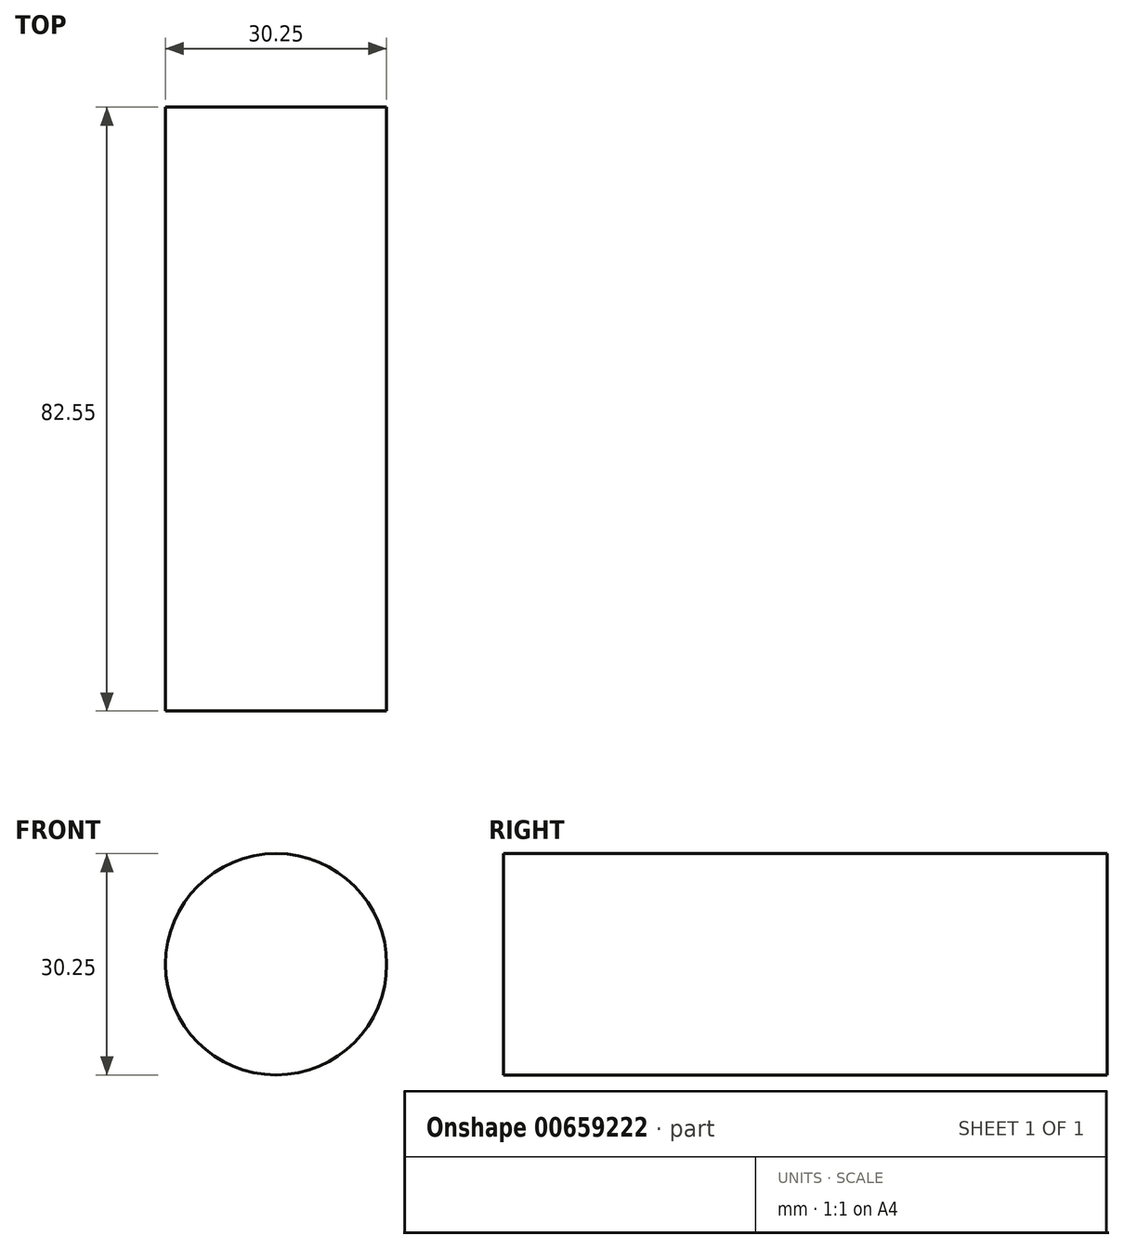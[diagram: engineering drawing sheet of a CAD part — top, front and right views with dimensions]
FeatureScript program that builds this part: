
annotation { "Feature Type Name" : "Feature", "Feature Type Description" : "" }
export const myFeature = defineFeature(function(context is Context, id is Id, definition is map)
    precondition{}
    {
        {
            var Q0;
            Q0=qCreatedBy(makeId("Front.planeOp"),FACE);
            var sketch = newSketch(context, id + "F0", { "sketchPlane" : qUnion([Q0])});
            skCircle(sketch, "E0", {"center": v(-76.53, 11.9) * mm, "radius": 15.12 * mm});
            skSolve(sketch);
        }
        {
            var Q0;
            Q0=makeQuery(id+"F0.imprint","IMPRINT",FACE,{"disambiguationData":[TD([[makeQuery(id+"F0.imprint","IMPRINT",EDGE,{"derivedFrom":sQuery(id+"F0.wireOp",EDGE,"E0")}),1.0]])]});
            extrude(context, id + "F1", {"entities" : qUnion([Q0]), "depth" : 82.55 * mm, "offsetDistance" : 25.4 * mm});
        }
    });
